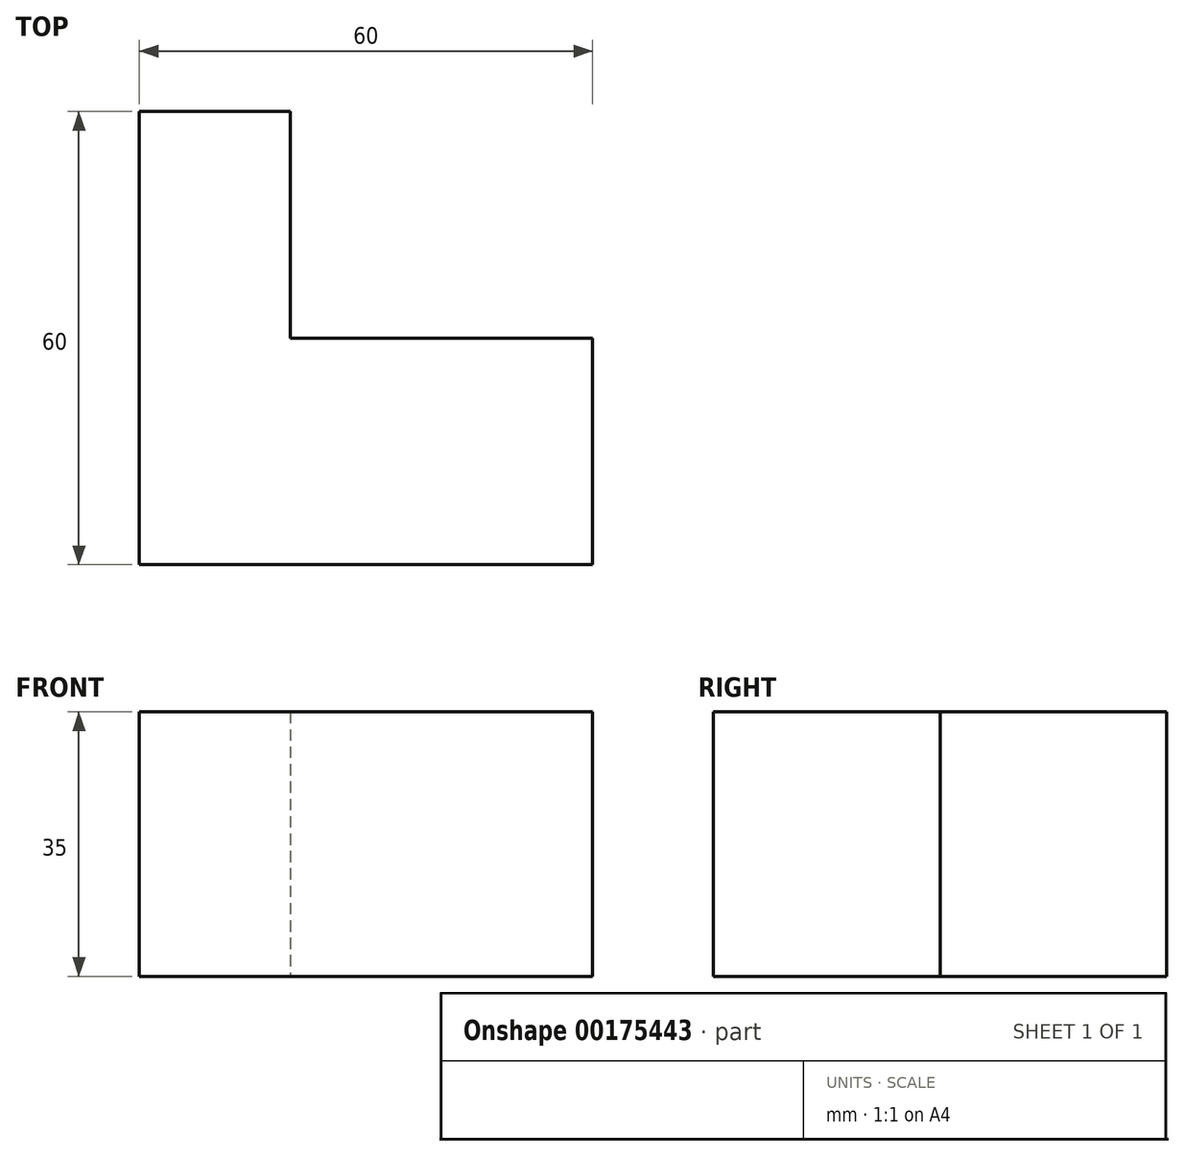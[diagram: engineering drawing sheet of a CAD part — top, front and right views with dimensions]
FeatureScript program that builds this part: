
annotation { "Feature Type Name" : "Feature", "Feature Type Description" : "" }
export const myFeature = defineFeature(function(context is Context, id is Id, definition is map)
    precondition{}
    {
        {
            var Q0;
            Q0=qCreatedBy(makeId("Top.planeOp"),FACE);
            var sketch = newSketch(context, id + "F0", { "sketchPlane" : qUnion([Q0])});
            skLineSegment(sketch, "E0.bottom", {"start": v(-6.36, 0) * mm, "end": v(33.64, 0) * mm});
            skLineSegment(sketch, "E0.top", {"start": v(-26.36, -30) * mm, "end": v(33.64, -30) * mm});
            skLineSegment(sketch, "E0.left", {"start": v(-26.36, 0) * mm, "end": v(-26.36, -30) * mm});
            skLineSegment(sketch, "E0.right", {"start": v(33.64, 0) * mm, "end": v(33.64, -30) * mm});
            skLineSegment(sketch, "E1", {"start": v(-26.36, 0) * mm, "end": v(-26.36, 30) * mm});
            skLineSegment(sketch, "E2", {"start": v(-26.36, 30) * mm, "end": v(-6.36, 30) * mm});
            skLineSegment(sketch, "E3", {"start": v(-6.36, 30) * mm, "end": v(-6.36, 0) * mm});
            skSolve(sketch);
        }
        {
            var Q0;
            Q0=makeQuery(id+"F0.imprint","IMPRINT",FACE,{"disambiguationData":[TD([[makeQuery(id+"F0.imprint","IMPRINT",EDGE,{"derivedFrom":sQuery(id+"F0.wireOp",EDGE,"E0.bottom")}),-1.0]])]});
            extrude(context, id + "F1", {"entities" : qUnion([Q0]), "depth" : 35 * mm});
        }
    });
